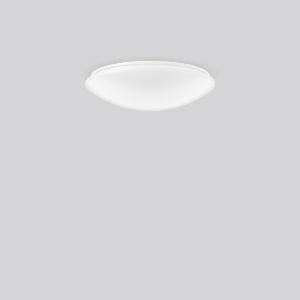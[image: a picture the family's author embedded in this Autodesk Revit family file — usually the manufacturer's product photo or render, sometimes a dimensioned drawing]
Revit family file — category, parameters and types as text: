
# Revit family: flat_polymero_311946_002_1_8544
name_source: partatom
category: Lighting Fixtures
units: mm (PartAtom-declared; Revit-internal decimal feet)

## family parameters
Cut with Voids When Loaded = No
Host = Face
Light Source = No
Part Type = Normal
Room Calculation Point = No
Round Connector Dimension = Use Diameter
Shared = No

## types (1)
- FLAT POLYMERO (1 x LED Modul 830, 2000 lm, 3000)
    Apparent Load = 19 VA
    CIE Flux Codes = 43 72 90 89 100
    Color Rendering = 80
    Color Temperature = 3000
    Default Elevation = 1800 mm
    Description = Series: FLAT POLYMERO
Decorative round surface-mounted luminaire. Base: metal, powder-coated. Diffuser made of non-yellowing plastic (PMMA), opal. Diffuser fastening: patented push system. Suitable for Ceiling mounting, Wall (surface). 
Colour: white
Diameter: 360 mm
Height: 100 mm
Lamp: LED exchangeable
Socket: without socket
Colour temperature: 3000K
Colour rendering index (CRI): 80
System power: 19 W
Rated luminous flux: 2000 lm
Beam angle Down: 117°
Luminous efficiency: 105 lm/W
Control gear: AC Strom, dim.Ph.an-/abschnitt
Protection class: I
Type of protection: IP 40
    Height = 100 mm  [stored 0.328084 ft]
    Lamp = 1 x LED Modul 830
    Lamp Light Flux = 2000 lm
    Lamp count = 1
    Length = 360 mm
    Lifetime = 50000 h
    Luminous efficacy = 105 lm/W
    Manufacturer = RZB
    ModVariant = No
    Model = 311946.002.1
    Mounting Place = Ceiling, Wall
    Mounting Type = Surface mounted
    Number of Poles = 1
    OnlyDefault = Yes
    Power Factor = 1
    Product Name = FLAT POLYMERO
    Product group = Surface mounted ceiling and wall luminaires
    ProductGroupID = 305
    Protection Class = Protection class I
    Protection Degree = IP 40
    RLX_Detail_Level = 1
    RLX_Emergency_Light_Flux = 0 lm
    RLX_Emergency_Type = 0
    RLX_Emergency_Type_DB = No
    RlxData = <blob elided: 76365 chars, md5=4f0afce2>
    Socket = socket
    Standby Power = 0 W
    System Light Flux = 2000 lm
    System Power = 19 W
    Type Comments = ALEA SPOT
    Type Image = 311523.002.1.jpg
    URL = http://relux.com
    VarID = ---
    Voltage = 230 V
    Voltage Range = 220-240 V
    Weight = 0.00 kg
    Width = 0 mm  [stored 0 ft]

note: [stored X ft] marks values corroborated as IEEE doubles in the binary element streams (Revit-internal decimal feet)

## geometry (parser evidence)
native form markers: Blend x4, Sweep x14
no freeform markers — native parametric forms only
